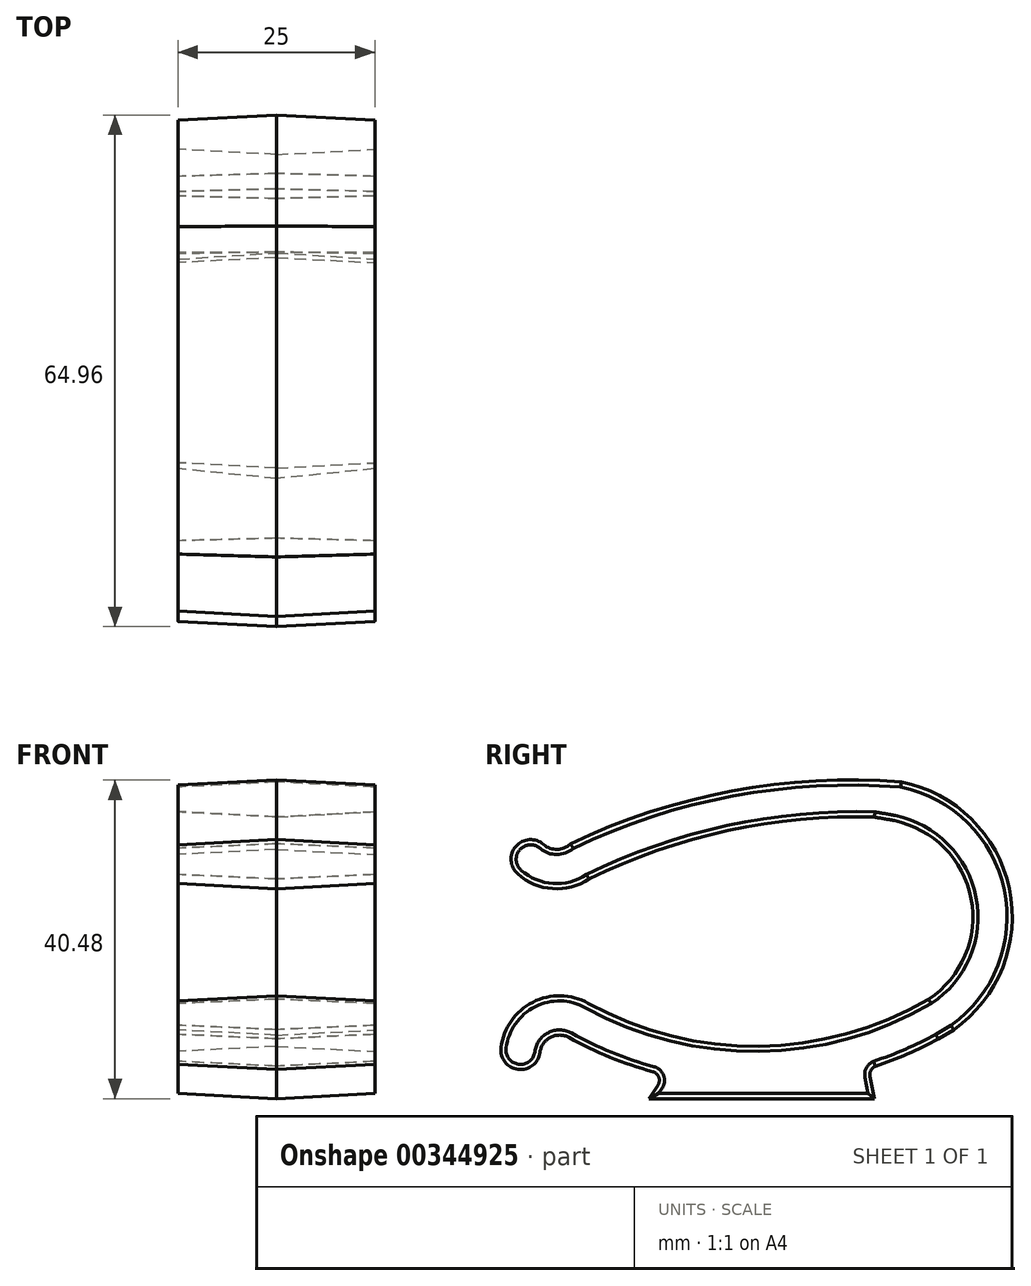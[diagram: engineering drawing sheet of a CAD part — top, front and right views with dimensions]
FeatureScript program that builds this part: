
annotation { "Feature Type Name" : "Feature", "Feature Type Description" : "" }
export const myFeature = defineFeature(function(context is Context, id is Id, definition is map)
    precondition{}
    {
        {
            var Q0;
            Q0=qCreatedBy(makeId("Right.planeOp"),FACE);
            var sketch = newSketch(context, id + "F0", { "sketchPlane" : qUnion([Q0])});
            skArc(sketch, "E0", {"start": v(21.37, 17.64) * mm, "mid": v(26.76, 30.44) * mm, "end": v(17, 40.32) * mm});
            skArc(sketch, "E1", {"start": v(-30.83, 33.53) * mm, "mid": v(-26.4, 31.68) * mm, "end": v(-21.77, 32.9) * mm});
            skArc(sketch, "E2", {"start": v(-21.88, 17.13) * mm, "mid": v(-28.9, 17.26) * mm, "end": v(-32.96, 11.51) * mm});
            skLineSegment(sketch, "E3", {"start": v(14.48, 44.42) * mm, "end": v(14.48, 2.4) * mm, "construction": true});
            skArc(sketch, "E4", {"start": v(17, 40.32) * mm, "mid": v(15.74, 40.56) * mm, "end": v(14.48, 40.77) * mm});
            skArc(sketch, "E5.0", {"start": v(-27.53, 37.29) * mm, "mid": v(-25.82, 36.67) * mm, "end": v(-24.15, 37.36) * mm});
            skArc(sketch, "E6", {"start": v(-27.53, 37.29) * mm, "mid": v(-31.06, 37.06) * mm, "end": v(-30.83, 33.53) * mm});
            skArc(sketch, "E7.0", {"start": v(-24.3, 12.76) * mm, "mid": v(-26.65, 12.8) * mm, "end": v(-28, 10.89) * mm});
            skArc(sketch, "E8", {"start": v(-32.96, 11.51) * mm, "mid": v(-30.8, 8.72) * mm, "end": v(-28, 10.89) * mm});
            skPoint(sketch, "E9.visualSharp", {"position": v(-8.28, 10.8) * mm});
            skPoint(sketch, "E10.visualSharp", {"position": v(7.92, 9.75) * mm});
            skArc(sketch, "E11", {"start": v(-21.88, 17.13) * mm, "mid": v(-0.2, 11.66) * mm, "end": v(21.37, 17.64) * mm});
            skArc(sketch, "E12.0", {"start": v(-24.3, 12.76) * mm, "mid": v(-19.12, 10.27) * mm, "end": v(-13.67, 8.42) * mm});
            skArc(sketch, "E13.0", {"start": v(24.56, 13.76) * mm, "mid": v(31.6, 31.7) * mm, "end": v(17.9, 45.23) * mm});
            skArc(sketch, "E14.trimOffspring", {"start": v(14.6, 9.12) * mm, "mid": v(18.67, 10.68) * mm, "end": v(22.6, 12.59) * mm});
            skPoint(sketch, "E15.visualSharp", {"position": v(-9.46, 7.45) * mm});
            skPoint(sketch, "E16.visualSharp", {"position": v(9.25, 7.68) * mm});
            skArc(sketch, "E17", {"start": v(-13.04, 6.68) * mm, "mid": v(-12.9, 7.7) * mm, "end": v(-13.67, 8.42) * mm});
            skArc(sketch, "E18", {"start": v(14.6, 9.12) * mm, "mid": v(14.03, 8.6) * mm, "end": v(13.92, 7.85) * mm});
            skLineSegment(sketch, "E19", {"start": v(14.48, 5) * mm, "end": v(-14.18, 5) * mm});
            skLineSegment(sketch, "E20", {"start": v(24.56, 13.76) * mm, "end": v(22.6, 12.59) * mm});
            skArc(sketch, "E21", {"start": v(14.48, 40.77) * mm, "mid": v(-4.12, 39.05) * mm, "end": v(-21.77, 32.9) * mm});
            skArc(sketch, "E22", {"start": v(17.9, 45.23) * mm, "mid": v(-3.64, 44.08) * mm, "end": v(-24.15, 37.36) * mm});
            skLineSegment(sketch, "E23", {"start": v(-14.18, 5) * mm, "end": v(-13.04, 6.68) * mm});
            skPoint(sketch, "E24.start.orphan", {"position": v(-14.18, 6.2) * mm});
            skLineSegment(sketch, "E25", {"start": v(14.48, 5) * mm, "end": v(13.92, 7.85) * mm});
            skSolve(sketch);
        }
        {
            var Q0;
            Q0 = qSketchRegion(id + "F0", true);
            var Q1;
            Q1=makeQuery(id+"F0.imprint","IMPRINT",FACE,{"disambiguationData":[TD([[makeQuery(id+"F0.imprint","IMPRINT",EDGE,{"derivedFrom":sQuery(id+"F0.wireOp",EDGE,"E0")}),-1.0]])]});
            extrude(context, id + "F1", {"entities" : qUnion([Q0, Q1]), "endBound" : BoundingType.SYMMETRIC, "depth" : 25 * mm, "hasDraft" : true, "draftAngle" : 3 * degree});
        }
        {
            var Q0;
            Q0=makeQuery(id+"F0.imprint","IMPRINT",FACE,{"disambiguationData":[TD([[makeQuery(id+"F0.imprint","IMPRINT",EDGE,{"derivedFrom":sQuery(id+"F0.wireOp",EDGE,"E0")}),-1.0]])]});
            var Q1;
            Q1=sQuery(id+"F0.wireOp",EDGE,"E22");
            var Q2;
            Q2=sQuery(id+"F0.wireOp",EDGE,"E0");
            var Q3;
            Q3=sQuery(id+"F0.wireOp",EDGE,"E13.0");
            var Q4;
            Q4=sQuery(id+"F0.wireOp",EDGE,"E14.trimOffspring");
            var Q5;
            Q5=sQuery(id+"F0.wireOp",EDGE,"E11");
            var Q6;
            Q6=sQuery(id+"F0.wireOp",EDGE,"E19");
            var Q7;
            Q7=sQuery(id+"F0.wireOp",EDGE,"E25");
            var Q8;
            Q8=sQuery(id+"F0.wireOp",EDGE,"E23");
            var Q9;
            Q9=sQuery(id+"F0.wireOp",EDGE,"E12.0");
            var Q10;
            Q10=sQuery(id+"F0.wireOp",EDGE,"E2");
            var Q11;
            Q11=sQuery(id+"F0.wireOp",EDGE,"E8");
            var Q12;
            Q12=sQuery(id+"F0.wireOp",EDGE,"E7.0");
            var Q13;
            Q13=sQuery(id+"F0.wireOp",EDGE,"E17");
            var Q14;
            Q14=sQuery(id+"F0.wireOp",EDGE,"E18");
            var Q15;
            Q15=sQuery(id+"F0.wireOp",EDGE,"E20");
            var Q16;
            Q16=sQuery(id+"F0.wireOp",EDGE,"E4");
            var Q17;
            Q17=sQuery(id+"F0.wireOp",EDGE,"E21");
            var Q18;
            Q18=sQuery(id+"F0.wireOp",EDGE,"E6");
            var Q19;
            Q19=sQuery(id+"F0.wireOp",EDGE,"E1");
            var Q20;
            Q20=sQuery(id+"F0.wireOp",EDGE,"E5.0");
            extrude(context, id + "F2", {"entities" : qUnion([Q0]), "operationType" : NewBodyOperationType.INTERSECT, "surfaceEntities" : qUnion([Q1, Q2, Q3, Q4, Q5, Q6, Q7, Q8, Q9, Q10, Q11, Q12, Q13, Q14, Q15, Q16, Q17, Q18, Q19, Q20]), "endBound" : BoundingType.SYMMETRIC, "depth" : 80 * mm, "hasDraft" : true, "draftAngle" : 3 * degree, "draftPullDirection" : true});
        }
    });
